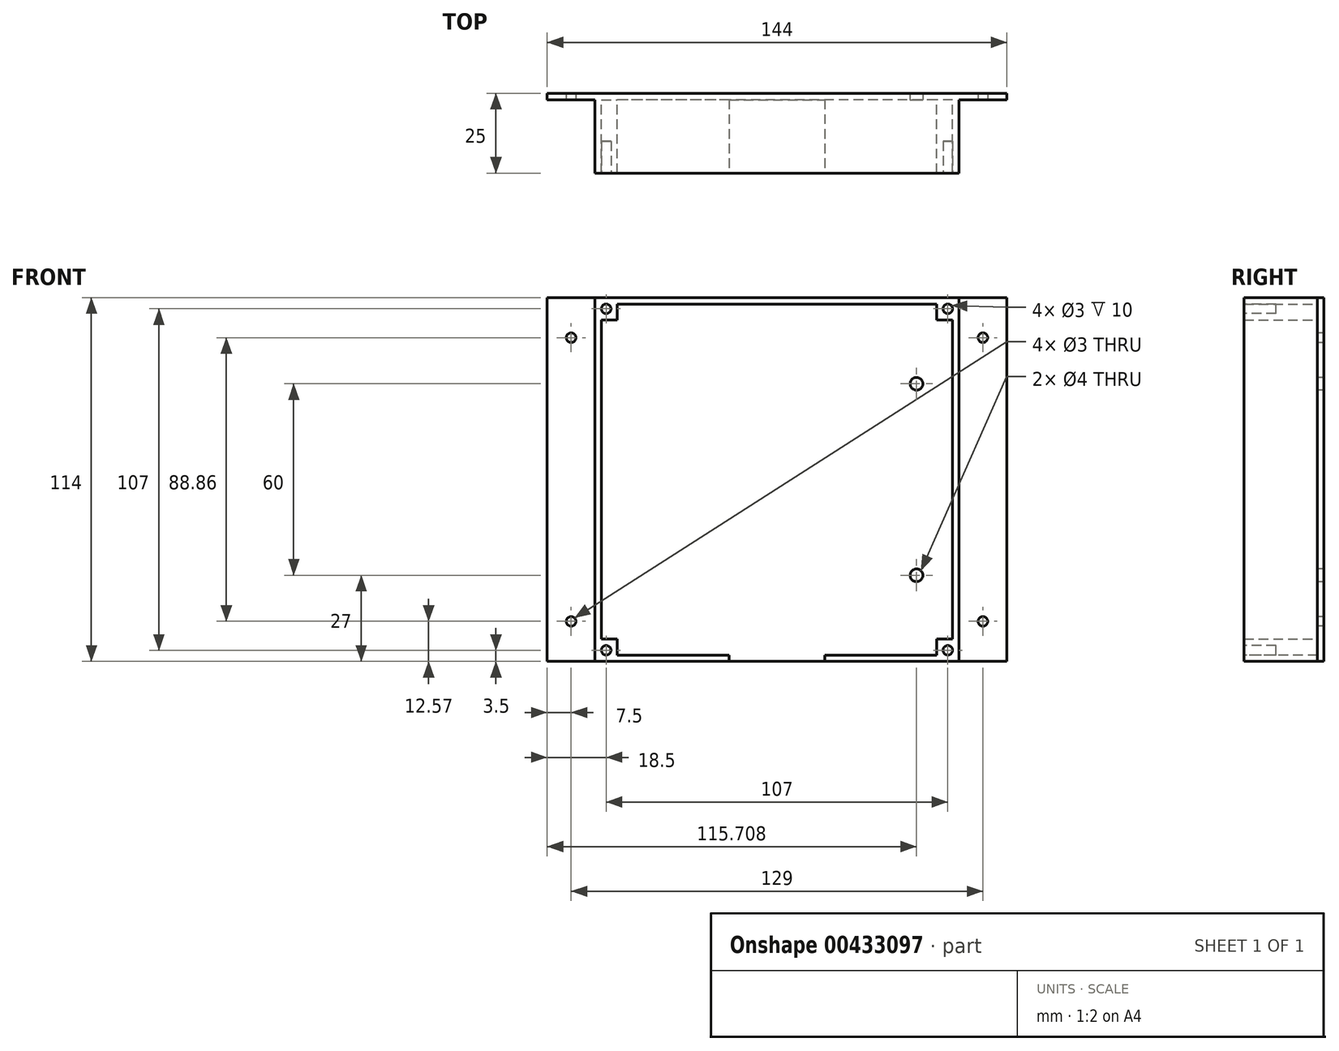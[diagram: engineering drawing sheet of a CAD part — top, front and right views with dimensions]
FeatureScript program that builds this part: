
annotation { "Feature Type Name" : "Feature", "Feature Type Description" : "" }
export const myFeature = defineFeature(function(context is Context, id is Id, definition is map)
    precondition{}
    {
        {
            var Q0;
            Q0=qCreatedBy(makeId("Front.planeOp"),FACE);
            var sketch = newSketch(context, id + "F0", { "sketchPlane" : qUnion([Q0])});
            skLineSegment(sketch, "E0.bottom", {"start": v(55, 55) * mm, "end": v(-55, 55) * mm});
            skLineSegment(sketch, "E0.top", {"start": v(55, -55) * mm, "end": v(-55, -55) * mm});
            skLineSegment(sketch, "E0.left", {"start": v(55, 55) * mm, "end": v(55, -55) * mm});
            skLineSegment(sketch, "E0.right", {"start": v(-55, 55) * mm, "end": v(-55, -55) * mm});
            skPoint(sketch, "E0.middle", {"position": v(0, 0) * mm});
            skSolve(sketch);
        }
        {
            var Q0;
            Q0 = qSketchRegion(id + "F0", true);
            extrude(context, id + "F1", {"entities" : qUnion([Q0]), "depth" : 2 * mm});
        }
        {
            var Q0;
            Q0=qCreatedBy(makeId("Front.planeOp"),FACE);
            var sketch = newSketch(context, id + "F2", { "sketchPlane" : qUnion([Q0])});
            skLineSegment(sketch, "E1.0.0", {"start": v(-55, -55) * mm, "end": v(55, -55) * mm, "construction": true});
            skLineSegment(sketch, "E1.0.1", {"start": v(55, -55) * mm, "end": v(55, 55) * mm, "construction": true});
            skLineSegment(sketch, "E1.0.2", {"start": v(55, 55) * mm, "end": v(-55, 55) * mm, "construction": true});
            skLineSegment(sketch, "E1.0.3", {"start": v(-55, 55) * mm, "end": v(-55, -55) * mm, "construction": true});
            skLineSegment(sketch, "E2.0", {"start": v(55, 57) * mm, "end": v(-55, 57) * mm});
            skLineSegment(sketch, "E3.0", {"start": v(57, -55) * mm, "end": v(57, 55) * mm});
            skLineSegment(sketch, "E4.0", {"start": v(-55, -57) * mm, "end": v(55, -57) * mm});
            skLineSegment(sketch, "E5.0", {"start": v(-57, 55) * mm, "end": v(-57, -55) * mm});
            skLineSegment(sketch, "E6", {"start": v(-57, 55) * mm, "end": v(-57, 57) * mm});
            skLineSegment(sketch, "E7", {"start": v(-57, 57) * mm, "end": v(-55, 57) * mm});
            skLineSegment(sketch, "E8.MirrorCS", {"start": v(57, 55) * mm, "end": v(57, 57) * mm});
            skLineSegment(sketch, "E9.MirrorCS", {"start": v(57, 57) * mm, "end": v(55, 57) * mm});
            skLineSegment(sketch, "E10.MirrorCS", {"start": v(-57, -55) * mm, "end": v(-57, -57) * mm});
            skLineSegment(sketch, "E11.MirrorCS", {"start": v(-57, -57) * mm, "end": v(-55, -57) * mm});
            skLineSegment(sketch, "E12.MirrorCS", {"start": v(57, -55) * mm, "end": v(57, -57) * mm});
            skLineSegment(sketch, "E13.MirrorCS", {"start": v(57, -57) * mm, "end": v(55, -57) * mm});
            skLineSegment(sketch, "E14.bottom", {"start": v(55, 55) * mm, "end": v(-55, 55) * mm});
            skLineSegment(sketch, "E14.top", {"start": v(55, -55) * mm, "end": v(-55, -55) * mm});
            skLineSegment(sketch, "E14.left", {"start": v(55, 55) * mm, "end": v(55, -55) * mm});
            skLineSegment(sketch, "E14.right", {"start": v(-55, 55) * mm, "end": v(-55, -55) * mm});
            skPoint(sketch, "E14.middle", {"position": v(0, 0) * mm});
            skSolve(sketch);
        }
        {
            var Q0;
            Q0 = qSketchRegion(id + "F2", true);
            extrude(context, id + "F3", {"entities" : qUnion([Q0]), "operationType" : NewBodyOperationType.ADD, "depth" : 25 * mm});
        }
        {
            var Q0;
            Q0=makeQuery(id+"F1.opExtrude","CAP_FACE",FACE,{"disambiguationData":[OSD([sQuery(id+"F0.wireOp",EDGE,"E0.bottom"),sQuery(id+"F0.wireOp",EDGE,"E0.top"),sQuery(id+"F0.wireOp",EDGE,"E0.left"),sQuery(id+"F0.wireOp",EDGE,"E0.right")])],"isStart":false});
            var sketch = newSketch(context, id + "F4", { "sketchPlane" : qUnion([Q0])});
            skLineSegment(sketch, "E15.bottom", {"start": v(-55, 55) * mm, "end": v(-50, 55) * mm});
            skLineSegment(sketch, "E15.top", {"start": v(-55, 50) * mm, "end": v(-50, 50) * mm});
            skLineSegment(sketch, "E15.left", {"start": v(-55, 55) * mm, "end": v(-55, 50) * mm});
            skLineSegment(sketch, "E15.right", {"start": v(-50, 55) * mm, "end": v(-50, 50) * mm});
            skLineSegment(sketch, "E16.0", {"start": v(57, 57) * mm, "end": v(-57, 57) * mm});
            skLineSegment(sketch, "E17", {"start": v(-57, 57) * mm, "end": v(-50, 50) * mm, "construction": true});
            skLineSegment(sketch, "E18.MirrorCS", {"start": v(50, 55) * mm, "end": v(50, 50) * mm});
            skLineSegment(sketch, "E19.MirrorCS", {"start": v(55, 50) * mm, "end": v(50, 50) * mm});
            skLineSegment(sketch, "E20.MirrorCS", {"start": v(-55, -50) * mm, "end": v(-50, -50) * mm});
            skLineSegment(sketch, "E21.MirrorCS", {"start": v(-50, -55) * mm, "end": v(-50, -50) * mm});
            skLineSegment(sketch, "E22.MirrorCS", {"start": v(55, -50) * mm, "end": v(50, -50) * mm});
            skLineSegment(sketch, "E23.MirrorCS", {"start": v(50, -55) * mm, "end": v(50, -50) * mm});
            skLineSegment(sketch, "E24.MirrorCS", {"start": v(-55, -55) * mm, "end": v(-50, -55) * mm});
            skLineSegment(sketch, "E25.MirrorCS", {"start": v(-55, -55) * mm, "end": v(-55, -50) * mm});
            skLineSegment(sketch, "E26.MirrorCS", {"start": v(55, 55) * mm, "end": v(55, 50) * mm});
            skLineSegment(sketch, "E27.MirrorCS", {"start": v(55, 55) * mm, "end": v(50, 55) * mm});
            skLineSegment(sketch, "E28.MirrorCS", {"start": v(55, -55) * mm, "end": v(50, -55) * mm});
            skLineSegment(sketch, "E29.MirrorCS", {"start": v(55, -55) * mm, "end": v(55, -50) * mm});
            skSolve(sketch);
        }
        {
            var Q0;
            Q0 = qSketchRegion(id + "F4", true);
            extrude(context, id + "F5", {"entities" : qUnion([Q0]), "operationType" : NewBodyOperationType.ADD, "depth" : 23 * mm});
        }
        {
            var Q0;
            Q0=makeQuery(id+"F5.boolean.opBoolean","MERGE",FACE,{"derivedFrom":[makeQuery(id+"F3.opExtrude","CAP_FACE",FACE,{"disambiguationData":[OSD([sQuery(id+"F2.wireOp",EDGE,"E2.0"),sQuery(id+"F2.wireOp",EDGE,"E3.0"),sQuery(id+"F2.wireOp",EDGE,"E4.0"),sQuery(id+"F2.wireOp",EDGE,"E5.0"),sQuery(id+"F2.wireOp",EDGE,"E6"),sQuery(id+"F2.wireOp",EDGE,"E7"),sQuery(id+"F2.wireOp",EDGE,"E8.MirrorCS"),sQuery(id+"F2.wireOp",EDGE,"E9.MirrorCS"),sQuery(id+"F2.wireOp",EDGE,"E10.MirrorCS"),sQuery(id+"F2.wireOp",EDGE,"E11.MirrorCS"),sQuery(id+"F2.wireOp",EDGE,"E12.MirrorCS"),sQuery(id+"F2.wireOp",EDGE,"E13.MirrorCS"),sQuery(id+"F2.wireOp",EDGE,"E14.bottom"),sQuery(id+"F2.wireOp",EDGE,"E14.top"),sQuery(id+"F2.wireOp",EDGE,"E14.left"),sQuery(id+"F2.wireOp",EDGE,"E14.right")])],"isStart":false}),makeQuery(id+"F5.opExtrude","CAP_FACE",FACE,{"disambiguationData":[OSD([sQuery(id+"F4.wireOp",EDGE,"E15.bottom"),sQuery(id+"F4.wireOp",EDGE,"E15.top"),sQuery(id+"F4.wireOp",EDGE,"E15.left"),sQuery(id+"F4.wireOp",EDGE,"E15.right")])],"isStart":false}),makeQuery(id+"F5.opExtrude","CAP_FACE",FACE,{"disambiguationData":[OSD([sQuery(id+"F4.wireOp",EDGE,"E18.MirrorCS"),sQuery(id+"F4.wireOp",EDGE,"E19.MirrorCS"),sQuery(id+"F4.wireOp",EDGE,"E26.MirrorCS"),sQuery(id+"F4.wireOp",EDGE,"E27.MirrorCS")])],"isStart":false}),makeQuery(id+"F5.opExtrude","CAP_FACE",FACE,{"disambiguationData":[OSD([sQuery(id+"F4.wireOp",EDGE,"E20.MirrorCS"),sQuery(id+"F4.wireOp",EDGE,"E21.MirrorCS"),sQuery(id+"F4.wireOp",EDGE,"E24.MirrorCS"),sQuery(id+"F4.wireOp",EDGE,"E25.MirrorCS")])],"isStart":false}),makeQuery(id+"F5.opExtrude","CAP_FACE",FACE,{"disambiguationData":[OSD([sQuery(id+"F4.wireOp",EDGE,"E22.MirrorCS"),sQuery(id+"F4.wireOp",EDGE,"E23.MirrorCS"),sQuery(id+"F4.wireOp",EDGE,"E28.MirrorCS"),sQuery(id+"F4.wireOp",EDGE,"E29.MirrorCS")])],"isStart":false})]});
            var sketch = newSketch(context, id + "F6", { "sketchPlane" : qUnion([Q0])});
            skLineSegment(sketch, "E30", {"start": v(-50, 50) * mm, "end": v(-57, 57) * mm, "construction": true});
            skCircle(sketch, "E31", {"center": v(-53.5, 53.5) * mm, "radius": 1.5 * mm});
            skCircle(sketch, "E32.MirrorC", {"center": v(53.5, 53.5) * mm, "radius": 1.5 * mm});
            skCircle(sketch, "E33.MirrorC", {"center": v(-53.5, -53.5) * mm, "radius": 1.5 * mm});
            skCircle(sketch, "E34.MirrorC", {"center": v(53.5, -53.5) * mm, "radius": 1.5 * mm});
            skSolve(sketch);
        }
        {
            var Q0;
            Q0 = qSketchRegion(id + "F6", true);
            extrude(context, id + "F7", {"entities" : qUnion([Q0]), "operationType" : NewBodyOperationType.REMOVE, "oppositeDirection" : true, "depth" : 10 * mm});
        }
        {
            var Q0;
            Q0=qCreatedBy(makeId("Front.planeOp"),FACE);
            var sketch = newSketch(context, id + "F8", { "sketchPlane" : qUnion([Q0])});
            skLineSegment(sketch, "E35.0", {"start": v(-57, -57) * mm, "end": v(-57, 57) * mm});
            skLineSegment(sketch, "E36.bottom", {"start": v(-57, 57) * mm, "end": v(-72, 57) * mm});
            skLineSegment(sketch, "E36.top", {"start": v(-57, -57) * mm, "end": v(-72, -57) * mm});
            skLineSegment(sketch, "E36.left", {"start": v(-57, 57) * mm, "end": v(-57, -57) * mm});
            skLineSegment(sketch, "E36.right", {"start": v(-72, 57) * mm, "end": v(-72, -57) * mm});
            skLineSegment(sketch, "E37.MirrorCS", {"start": v(57, -57) * mm, "end": v(57, 57) * mm});
            skLineSegment(sketch, "E38.MirrorCS", {"start": v(57, 57) * mm, "end": v(72, 57) * mm});
            skLineSegment(sketch, "E39.MirrorCS", {"start": v(72, 57) * mm, "end": v(72, -57) * mm});
            skLineSegment(sketch, "E40.MirrorCS", {"start": v(57, -57) * mm, "end": v(72, -57) * mm});
            skSolve(sketch);
        }
        {
            var Q0;
            Q0 = qSketchRegion(id + "F8", true);
            extrude(context, id + "F9", {"entities" : qUnion([Q0]), "operationType" : NewBodyOperationType.ADD, "depth" : 2 * mm});
        }
        {
            var Q0;
            Q0=makeQuery(id+"F9.opExtrude","CAP_FACE",FACE,{"disambiguationData":[OSD([sQuery(id+"F8.wireOp",EDGE,"E36.bottom"),sQuery(id+"F8.wireOp",EDGE,"E36.top"),sQuery(id+"F8.wireOp",EDGE,"E36.left"),sQuery(id+"F8.wireOp",EDGE,"E36.right")])],"isStart":false});
            var sketch = newSketch(context, id + "F10", { "sketchPlane" : qUnion([Q0])});
            skCircle(sketch, "E41", {"center": v(-64.5, 44.43) * mm, "radius": 1.5 * mm});
            skPoint(sketch, "E41.centerSnap0", {"position": v(-64.5, 57) * mm});
            skCircle(sketch, "E42.MirrorC", {"center": v(64.5, 44.43) * mm, "radius": 1.5 * mm});
            skCircle(sketch, "E43.MirrorC", {"center": v(-64.5, -44.43) * mm, "radius": 1.5 * mm});
            skCircle(sketch, "E44.MirrorC", {"center": v(64.5, -44.43) * mm, "radius": 1.5 * mm});
            skSolve(sketch);
        }
        {
            var Q0;
            Q0 = qSketchRegion(id + "F10", true);
            extrude(context, id + "F11", {"entities" : qUnion([Q0]), "operationType" : NewBodyOperationType.REMOVE, "endBound" : BoundingType.THROUGH_ALL, "oppositeDirection" : true, "depth" : 25 * mm});
        }
        {
            var Q0;
            Q0=makeQuery(id+"F5.boolean.opBoolean","MERGE",FACE,{"derivedFrom":[makeQuery(id+"F3.opExtrude","CAP_FACE",FACE,{"disambiguationData":[OSD([sQuery(id+"F2.wireOp",EDGE,"E2.0"),sQuery(id+"F2.wireOp",EDGE,"E3.0"),sQuery(id+"F2.wireOp",EDGE,"E4.0"),sQuery(id+"F2.wireOp",EDGE,"E5.0"),sQuery(id+"F2.wireOp",EDGE,"E6"),sQuery(id+"F2.wireOp",EDGE,"E7"),sQuery(id+"F2.wireOp",EDGE,"E8.MirrorCS"),sQuery(id+"F2.wireOp",EDGE,"E9.MirrorCS"),sQuery(id+"F2.wireOp",EDGE,"E10.MirrorCS"),sQuery(id+"F2.wireOp",EDGE,"E11.MirrorCS"),sQuery(id+"F2.wireOp",EDGE,"E12.MirrorCS"),sQuery(id+"F2.wireOp",EDGE,"E13.MirrorCS"),sQuery(id+"F2.wireOp",EDGE,"E14.bottom"),sQuery(id+"F2.wireOp",EDGE,"E14.top"),sQuery(id+"F2.wireOp",EDGE,"E14.left"),sQuery(id+"F2.wireOp",EDGE,"E14.right")])],"isStart":false}),makeQuery(id+"F5.opExtrude","CAP_FACE",FACE,{"disambiguationData":[OSD([sQuery(id+"F4.wireOp",EDGE,"E15.bottom"),sQuery(id+"F4.wireOp",EDGE,"E15.top"),sQuery(id+"F4.wireOp",EDGE,"E15.left"),sQuery(id+"F4.wireOp",EDGE,"E15.right")])],"isStart":false}),makeQuery(id+"F5.opExtrude","CAP_FACE",FACE,{"disambiguationData":[OSD([sQuery(id+"F4.wireOp",EDGE,"E18.MirrorCS"),sQuery(id+"F4.wireOp",EDGE,"E19.MirrorCS"),sQuery(id+"F4.wireOp",EDGE,"E26.MirrorCS"),sQuery(id+"F4.wireOp",EDGE,"E27.MirrorCS")])],"isStart":false}),makeQuery(id+"F5.opExtrude","CAP_FACE",FACE,{"disambiguationData":[OSD([sQuery(id+"F4.wireOp",EDGE,"E20.MirrorCS"),sQuery(id+"F4.wireOp",EDGE,"E21.MirrorCS"),sQuery(id+"F4.wireOp",EDGE,"E24.MirrorCS"),sQuery(id+"F4.wireOp",EDGE,"E25.MirrorCS")])],"isStart":false}),makeQuery(id+"F5.opExtrude","CAP_FACE",FACE,{"disambiguationData":[OSD([sQuery(id+"F4.wireOp",EDGE,"E22.MirrorCS"),sQuery(id+"F4.wireOp",EDGE,"E23.MirrorCS"),sQuery(id+"F4.wireOp",EDGE,"E28.MirrorCS"),sQuery(id+"F4.wireOp",EDGE,"E29.MirrorCS")])],"isStart":false})]});
            var sketch = newSketch(context, id + "F12", { "sketchPlane" : qUnion([Q0])});
            skLineSegment(sketch, "E45", {"start": v(-15, -55) * mm, "end": v(15, -55) * mm});
            skLineSegment(sketch, "E46", {"start": v(15, -55) * mm, "end": v(15, -57) * mm});
            skLineSegment(sketch, "E47", {"start": v(15, -57) * mm, "end": v(-15, -57) * mm});
            skLineSegment(sketch, "E48", {"start": v(-15, -57) * mm, "end": v(-15, -55) * mm});
            skSolve(sketch);
        }
        {
            var Q0;
            Q0 = qSketchRegion(id + "F12", true);
            extrude(context, id + "F13", {"entities" : qUnion([Q0]), "operationType" : NewBodyOperationType.REMOVE, "oppositeDirection" : true, "depth" : 23 * mm});
        }
        {
            var Q0;
            Q0=makeQuery(id+"F13.boolean.opBoolean","MERGE",FACE,{"derivedFrom":[makeQuery(id+"F1.opExtrude","CAP_FACE",FACE,{"disambiguationData":[OSD([sQuery(id+"F0.wireOp",EDGE,"E0.bottom"),sQuery(id+"F0.wireOp",EDGE,"E0.top"),sQuery(id+"F0.wireOp",EDGE,"E0.left"),sQuery(id+"F0.wireOp",EDGE,"E0.right")])],"isStart":false}),makeQuery(id+"F13.opExtrude","CAP_FACE",FACE,{"disambiguationData":[OSD([sQuery(id+"F12.wireOp",EDGE,"E45"),sQuery(id+"F12.wireOp",EDGE,"E46"),sQuery(id+"F12.wireOp",EDGE,"E47"),sQuery(id+"F12.wireOp",EDGE,"E48")])],"isStart":false})]});
            var sketch = newSketch(context, id + "F14", { "sketchPlane" : qUnion([Q0])});
            skCircle(sketch, "E49", {"center": v(43.7, 30) * mm, "radius": 2 * mm});
            skCircle(sketch, "E50.MirrorC", {"center": v(43.7, -30) * mm, "radius": 2 * mm});
            skSolve(sketch);
        }
        {
            var Q0;
            Q0 = qSketchRegion(id + "F14", true);
            extrude(context, id + "F15", {"entities" : qUnion([Q0]), "operationType" : NewBodyOperationType.REMOVE, "endBound" : BoundingType.THROUGH_ALL, "oppositeDirection" : true, "depth" : 25 * mm});
        }
    });
